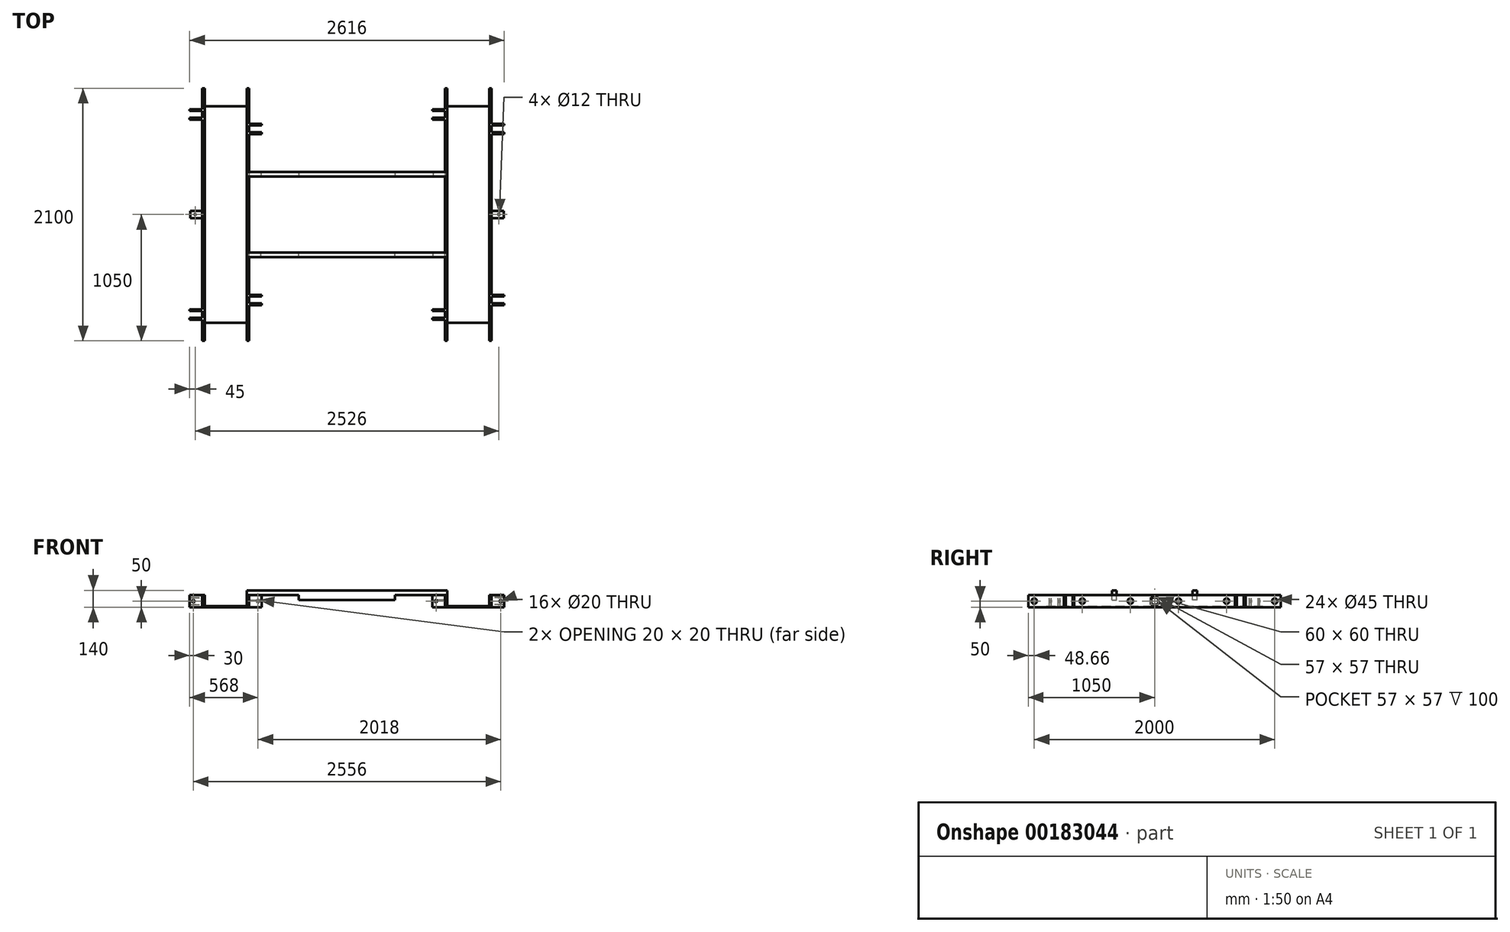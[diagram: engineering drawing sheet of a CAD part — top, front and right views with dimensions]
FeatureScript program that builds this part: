
annotation { "Feature Type Name" : "Feature", "Feature Type Description" : "" }
export const myFeature = defineFeature(function(context is Context, id is Id, definition is map)
    precondition{}
    {
        {
            var Q0;
            Q0=qCreatedBy(makeId("Front.planeOp"),FACE);
            var sketch = newSketch(context, id + "F0", { "sketchPlane" : qUnion([Q0])});
            skLineSegment(sketch, "E0", {"start": v(0, 0) * mm, "end": v(-815, 0) * mm, "construction": true});
            skLineSegment(sketch, "E1", {"start": v(0, 0) * mm, "end": v(815, 0) * mm, "construction": true});
            skLineSegment(sketch, "E2", {"start": v(-834, -90) * mm, "end": v(-1184, -90) * mm});
            skLineSegment(sketch, "E3", {"start": v(-1184, -90) * mm, "end": v(-1184, 0) * mm});
            skLineSegment(sketch, "E4", {"start": v(-1184, 0) * mm, "end": v(-1203, 0) * mm});
            skLineSegment(sketch, "E5", {"start": v(-1203, 0) * mm, "end": v(-1203, -100) * mm});
            skLineSegment(sketch, "E6", {"start": v(-1203, -100) * mm, "end": v(-815, -100) * mm});
            skLineSegment(sketch, "E7", {"start": v(-815, -100) * mm, "end": v(-815, 0) * mm});
            skLineSegment(sketch, "E8", {"start": v(-834, -90) * mm, "end": v(-834, 0) * mm});
            skLineSegment(sketch, "E9", {"start": v(-834, 0) * mm, "end": v(-815, 0) * mm});
            skLineSegment(sketch, "E10.MirrorCS", {"start": v(815, -100) * mm, "end": v(815, 0) * mm});
            skLineSegment(sketch, "E11.MirrorCS", {"start": v(834, -90) * mm, "end": v(834, 0) * mm});
            skLineSegment(sketch, "E12.MirrorCS", {"start": v(1203, -100) * mm, "end": v(815, -100) * mm});
            skLineSegment(sketch, "E13.MirrorCS", {"start": v(834, -90) * mm, "end": v(1184, -90) * mm});
            skLineSegment(sketch, "E14.MirrorCS", {"start": v(1184, -90) * mm, "end": v(1184, 0) * mm});
            skLineSegment(sketch, "E15.MirrorCS", {"start": v(1184, 0) * mm, "end": v(1203, 0) * mm});
            skLineSegment(sketch, "E16.MirrorCS", {"start": v(1203, 0) * mm, "end": v(1203, -100) * mm});
            skLineSegment(sketch, "E17.MirrorCS", {"start": v(834, 0) * mm, "end": v(815, 0) * mm});
            skSolve(sketch);
        }
        {
            var Q0;
            Q0=makeQuery(id+"F0.imprint","IMPRINT",FACE,{"disambiguationData":[TD([[makeQuery(id+"F0.imprint","IMPRINT",EDGE,{"derivedFrom":sQuery(id+"F0.wireOp",EDGE,"E2")}),1.0]])]});
            var Q1;
            Q1=makeQuery(id+"F0.imprint","IMPRINT",FACE,{"disambiguationData":[TD([[makeQuery(id+"F0.imprint","IMPRINT",EDGE,{"derivedFrom":sQuery(id+"F0.wireOp",EDGE,"E10.MirrorCS")}),-1.0]])]});
            extrude(context, id + "F1", {"entities" : qUnion([Q0, Q1]), "endBound" : BoundingType.SYMMETRIC, "depth" : 2100 * mm});
        }
        {
            var Q0;
            Q0=makeQuery(id+"F1.opExtrude","SWEPT_FACE",FACE,{"disambiguationData":[OSD([sQuery(id+"F0.wireOp",EDGE,"E9")])]});
            var sketch = newSketch(context, id + "F2", { "sketchPlane" : qUnion([Q0])});
            skLineSegment(sketch, "E18.bottom", {"start": v(-834, -355) * mm, "end": v(834, -355) * mm});
            skLineSegment(sketch, "E18.top", {"start": v(-834, -315) * mm, "end": v(834, -315) * mm});
            skLineSegment(sketch, "E18.left", {"start": v(834, -315) * mm, "end": v(834, -355) * mm});
            skLineSegment(sketch, "E18.right", {"start": v(-834, -315) * mm, "end": v(-834, -355) * mm});
            skLineSegment(sketch, "E19.bottom", {"start": v(-834, 315) * mm, "end": v(834, 315) * mm});
            skLineSegment(sketch, "E19.top", {"start": v(-834, 355) * mm, "end": v(834, 355) * mm});
            skLineSegment(sketch, "E19.left", {"start": v(-834, 355) * mm, "end": v(-834, 315) * mm});
            skLineSegment(sketch, "E19.right", {"start": v(834, 355) * mm, "end": v(834, 315) * mm});
            skSolve(sketch);
        }
        {
            var Q0;
            {var subQ0=sQuery(id+"F2.wireOp",EDGE,"E18.right");Q0=makeQuery(id+"F2.imprint","IMPRINT",FACE,{"disambiguationData":[TD([[makeQuery(id+"F2.imprint","IMPRINT",EDGE,{"derivedFrom":subQ0}),-1.0]])]});}
            var Q1;
            {var subQ0=sQuery(id+"F2.wireOp",EDGE,"E19.left");Q1=makeQuery(id+"F2.imprint","IMPRINT",FACE,{"disambiguationData":[TD([[makeQuery(id+"F2.imprint","IMPRINT",EDGE,{"derivedFrom":subQ0}),-1.0]])]});}
            var Q2;
            {var subQ0=sQuery(id+"F2.wireOp",EDGE,"E18.left");Q2=makeQuery(id+"F2.imprint","IMPRINT",FACE,{"disambiguationData":[TD([[makeQuery(id+"F2.imprint","IMPRINT",EDGE,{"derivedFrom":subQ0}),-1.0]])]});}
            var Q3;
            {var subQ0=sQuery(id+"F2.wireOp",EDGE,"E19.right");Q3=makeQuery(id+"F2.imprint","IMPRINT",FACE,{"disambiguationData":[TD([[makeQuery(id+"F2.imprint","IMPRINT",EDGE,{"derivedFrom":subQ0}),-1.0]])]});}
            extrude(context, id + "F3", {"entities" : qUnion([Q0, Q1, Q2, Q3]), "operationType" : NewBodyOperationType.ADD, "depth" : 40 * mm});
        }
        {
            var Q0;
            Q0=qCreatedBy(makeId("Top.planeOp"),FACE);
            var sketch = newSketch(context, id + "F4", { "sketchPlane" : qUnion([Q0])});
            skLineSegment(sketch, "E20.bottom", {"start": v(1203, 860) * mm, "end": v(1308, 860) * mm});
            skLineSegment(sketch, "E20.top", {"start": v(1203, 875) * mm, "end": v(1308, 875) * mm});
            skLineSegment(sketch, "E20.left", {"start": v(1203, 860) * mm, "end": v(1203, 875) * mm});
            skLineSegment(sketch, "E20.right", {"start": v(1308, 860) * mm, "end": v(1308, 875) * mm});
            skLineSegment(sketch, "E21.bottom", {"start": v(1203, 803) * mm, "end": v(1308, 803) * mm});
            skLineSegment(sketch, "E21.top", {"start": v(1203, 788) * mm, "end": v(1308, 788) * mm});
            skLineSegment(sketch, "E21.left", {"start": v(1203, 803) * mm, "end": v(1203, 788) * mm});
            skLineSegment(sketch, "E21.right", {"start": v(1308, 803) * mm, "end": v(1308, 788) * mm});
            skLineSegment(sketch, "E22.bottom", {"start": v(815, 755) * mm, "end": v(710, 755) * mm});
            skLineSegment(sketch, "E22.top", {"start": v(815, 740) * mm, "end": v(710, 740) * mm});
            skLineSegment(sketch, "E22.left", {"start": v(815, 755) * mm, "end": v(815, 740) * mm});
            skLineSegment(sketch, "E22.right", {"start": v(710, 755) * mm, "end": v(710, 740) * mm});
            skLineSegment(sketch, "E23.bottom", {"start": v(815, 668) * mm, "end": v(710, 668) * mm});
            skLineSegment(sketch, "E23.top", {"start": v(815, 683) * mm, "end": v(710, 683) * mm});
            skLineSegment(sketch, "E23.left", {"start": v(815, 668) * mm, "end": v(815, 683) * mm});
            skLineSegment(sketch, "E23.right", {"start": v(710, 668) * mm, "end": v(710, 683) * mm});
            skLineSegment(sketch, "E24.MirrorCS", {"start": v(-815, 683) * mm, "end": v(-710, 683) * mm});
            skLineSegment(sketch, "E25.MirrorCS", {"start": v(-815, 668) * mm, "end": v(-710, 668) * mm});
            skLineSegment(sketch, "E26.MirrorCS", {"start": v(-710, 668) * mm, "end": v(-710, 683) * mm});
            skLineSegment(sketch, "E27.MirrorCS", {"start": v(-815, 668) * mm, "end": v(-815, 683) * mm});
            skLineSegment(sketch, "E28.MirrorCS", {"start": v(-815, 755) * mm, "end": v(-815, 740) * mm});
            skLineSegment(sketch, "E29.MirrorCS", {"start": v(-815, 755) * mm, "end": v(-710, 755) * mm});
            skLineSegment(sketch, "E30.MirrorCS", {"start": v(-815, 740) * mm, "end": v(-710, 740) * mm});
            skLineSegment(sketch, "E31.MirrorCS", {"start": v(-710, 755) * mm, "end": v(-710, 740) * mm});
            skLineSegment(sketch, "E32.MirrorCS", {"start": v(-1203, 803) * mm, "end": v(-1203, 788) * mm});
            skLineSegment(sketch, "E33.MirrorCS", {"start": v(-1203, 803) * mm, "end": v(-1308, 803) * mm});
            skLineSegment(sketch, "E34.MirrorCS", {"start": v(-1203, 788) * mm, "end": v(-1308, 788) * mm});
            skLineSegment(sketch, "E35.MirrorCS", {"start": v(-1308, 803) * mm, "end": v(-1308, 788) * mm});
            skLineSegment(sketch, "E36.MirrorCS", {"start": v(-1308, 860) * mm, "end": v(-1308, 875) * mm});
            skLineSegment(sketch, "E37.MirrorCS", {"start": v(-1203, 860) * mm, "end": v(-1308, 860) * mm});
            skLineSegment(sketch, "E38.MirrorCS", {"start": v(-1203, 875) * mm, "end": v(-1308, 875) * mm});
            skLineSegment(sketch, "E39.MirrorCS", {"start": v(-1203, 860) * mm, "end": v(-1203, 875) * mm});
            skLineSegment(sketch, "E40", {"start": v(1009, 1050) * mm, "end": v(1009, 82.46) * mm, "construction": true});
            skLineSegment(sketch, "E41.MirrorCS", {"start": v(815, 860) * mm, "end": v(815, 875) * mm});
            skLineSegment(sketch, "E42.MirrorCS", {"start": v(815, 875) * mm, "end": v(710, 875) * mm});
            skLineSegment(sketch, "E43.MirrorCS", {"start": v(710, 860) * mm, "end": v(710, 875) * mm});
            skLineSegment(sketch, "E44.MirrorCS", {"start": v(815, 860) * mm, "end": v(710, 860) * mm});
            skLineSegment(sketch, "E45.MirrorCS", {"start": v(710, 803) * mm, "end": v(710, 788) * mm});
            skLineSegment(sketch, "E46.MirrorCS", {"start": v(815, 803) * mm, "end": v(710, 803) * mm});
            skLineSegment(sketch, "E47.MirrorCS", {"start": v(815, 788) * mm, "end": v(710, 788) * mm});
            skLineSegment(sketch, "E48.MirrorCS", {"start": v(815, 803) * mm, "end": v(815, 788) * mm});
            skLineSegment(sketch, "E49.MirrorCS", {"start": v(1203, 755) * mm, "end": v(1308, 755) * mm});
            skLineSegment(sketch, "E50.MirrorCS", {"start": v(1203, 740) * mm, "end": v(1308, 740) * mm});
            skLineSegment(sketch, "E51.MirrorCS", {"start": v(1203, 755) * mm, "end": v(1203, 740) * mm});
            skLineSegment(sketch, "E52.MirrorCS", {"start": v(1308, 755) * mm, "end": v(1308, 740) * mm});
            skLineSegment(sketch, "E53.MirrorCS", {"start": v(1308, 668) * mm, "end": v(1308, 683) * mm});
            skLineSegment(sketch, "E54.MirrorCS", {"start": v(1203, 683) * mm, "end": v(1308, 683) * mm});
            skLineSegment(sketch, "E55.MirrorCS", {"start": v(1203, 668) * mm, "end": v(1308, 668) * mm});
            skLineSegment(sketch, "E56.MirrorCS", {"start": v(1203, 668) * mm, "end": v(1203, 683) * mm});
            skLineSegment(sketch, "E57.MirrorCS", {"start": v(-815, 860) * mm, "end": v(-710, 860) * mm});
            skLineSegment(sketch, "E58.MirrorCS", {"start": v(-815, 875) * mm, "end": v(-710, 875) * mm});
            skLineSegment(sketch, "E59.MirrorCS", {"start": v(-815, 860) * mm, "end": v(-815, 875) * mm});
            skLineSegment(sketch, "E60.MirrorCS", {"start": v(-710, 860) * mm, "end": v(-710, 875) * mm});
            skLineSegment(sketch, "E61.MirrorCS", {"start": v(-710, 803) * mm, "end": v(-710, 788) * mm});
            skLineSegment(sketch, "E62.MirrorCS", {"start": v(-815, 803) * mm, "end": v(-710, 803) * mm});
            skLineSegment(sketch, "E63.MirrorCS", {"start": v(-815, 788) * mm, "end": v(-710, 788) * mm});
            skLineSegment(sketch, "E64.MirrorCS", {"start": v(-815, 803) * mm, "end": v(-815, 788) * mm});
            skLineSegment(sketch, "E65.MirrorCS", {"start": v(-1203, 668) * mm, "end": v(-1308, 668) * mm});
            skLineSegment(sketch, "E66.MirrorCS", {"start": v(-1203, 668) * mm, "end": v(-1203, 683) * mm});
            skLineSegment(sketch, "E67.MirrorCS", {"start": v(-1203, 683) * mm, "end": v(-1308, 683) * mm});
            skLineSegment(sketch, "E68.MirrorCS", {"start": v(-1308, 668) * mm, "end": v(-1308, 683) * mm});
            skLineSegment(sketch, "E69.MirrorCS", {"start": v(-1203, 740) * mm, "end": v(-1308, 740) * mm});
            skLineSegment(sketch, "E70.MirrorCS", {"start": v(-1203, 755) * mm, "end": v(-1308, 755) * mm});
            skLineSegment(sketch, "E71.MirrorCS", {"start": v(-1308, 755) * mm, "end": v(-1308, 740) * mm});
            skLineSegment(sketch, "E72.MirrorCS", {"start": v(-1203, 755) * mm, "end": v(-1203, 740) * mm});
            skLineSegment(sketch, "E73.MirrorCS", {"start": v(710, -755) * mm, "end": v(710, -740) * mm});
            skLineSegment(sketch, "E74.MirrorCS", {"start": v(815, -668) * mm, "end": v(815, -683) * mm});
            skLineSegment(sketch, "E75.MirrorCS", {"start": v(710, -803) * mm, "end": v(710, -788) * mm});
            skLineSegment(sketch, "E76.MirrorCS", {"start": v(710, -668) * mm, "end": v(710, -683) * mm});
            skLineSegment(sketch, "E77.MirrorCS", {"start": v(815, -755) * mm, "end": v(815, -740) * mm});
            skLineSegment(sketch, "E78.MirrorCS", {"start": v(815, -860) * mm, "end": v(815, -875) * mm});
            skLineSegment(sketch, "E79.MirrorCS", {"start": v(815, -803) * mm, "end": v(815, -788) * mm});
            skLineSegment(sketch, "E80.MirrorCS", {"start": v(710, -860) * mm, "end": v(710, -875) * mm});
            skLineSegment(sketch, "E81.MirrorCS", {"start": v(815, -668) * mm, "end": v(710, -668) * mm});
            skLineSegment(sketch, "E82.MirrorCS", {"start": v(815, -683) * mm, "end": v(710, -683) * mm});
            skLineSegment(sketch, "E83.MirrorCS", {"start": v(815, -788) * mm, "end": v(710, -788) * mm});
            skLineSegment(sketch, "E84.MirrorCS", {"start": v(815, -740) * mm, "end": v(710, -740) * mm});
            skLineSegment(sketch, "E85.MirrorCS", {"start": v(815, -755) * mm, "end": v(710, -755) * mm});
            skLineSegment(sketch, "E86.MirrorCS", {"start": v(815, -803) * mm, "end": v(710, -803) * mm});
            skLineSegment(sketch, "E87.MirrorCS", {"start": v(815, -860) * mm, "end": v(710, -860) * mm});
            skLineSegment(sketch, "E88.MirrorCS", {"start": v(815, -875) * mm, "end": v(710, -875) * mm});
            skLineSegment(sketch, "E89.MirrorCS", {"start": v(1308, -755) * mm, "end": v(1308, -740) * mm});
            skLineSegment(sketch, "E90.MirrorCS", {"start": v(1308, -803) * mm, "end": v(1308, -788) * mm});
            skLineSegment(sketch, "E91.MirrorCS", {"start": v(1308, -860) * mm, "end": v(1308, -875) * mm});
            skLineSegment(sketch, "E92.MirrorCS", {"start": v(1203, -860) * mm, "end": v(1203, -875) * mm});
            skLineSegment(sketch, "E93.MirrorCS", {"start": v(1203, -755) * mm, "end": v(1203, -740) * mm});
            skLineSegment(sketch, "E94.MirrorCS", {"start": v(1308, -668) * mm, "end": v(1308, -683) * mm});
            skLineSegment(sketch, "E95.MirrorCS", {"start": v(1203, -803) * mm, "end": v(1203, -788) * mm});
            skLineSegment(sketch, "E96.MirrorCS", {"start": v(1203, -668) * mm, "end": v(1203, -683) * mm});
            skLineSegment(sketch, "E97.MirrorCS", {"start": v(1203, -668) * mm, "end": v(1308, -668) * mm});
            skLineSegment(sketch, "E98.MirrorCS", {"start": v(1203, -788) * mm, "end": v(1308, -788) * mm});
            skLineSegment(sketch, "E99.MirrorCS", {"start": v(1203, -803) * mm, "end": v(1308, -803) * mm});
            skLineSegment(sketch, "E100.MirrorCS", {"start": v(1203, -755) * mm, "end": v(1308, -755) * mm});
            skLineSegment(sketch, "E101.MirrorCS", {"start": v(1203, -875) * mm, "end": v(1308, -875) * mm});
            skLineSegment(sketch, "E102.MirrorCS", {"start": v(1203, -860) * mm, "end": v(1308, -860) * mm});
            skLineSegment(sketch, "E103.MirrorCS", {"start": v(1203, -740) * mm, "end": v(1308, -740) * mm});
            skLineSegment(sketch, "E104.MirrorCS", {"start": v(1203, -683) * mm, "end": v(1308, -683) * mm});
            skLineSegment(sketch, "E105.MirrorCS", {"start": v(-1203, -860) * mm, "end": v(-1203, -875) * mm});
            skLineSegment(sketch, "E106.MirrorCS", {"start": v(-1308, -860) * mm, "end": v(-1308, -875) * mm});
            skLineSegment(sketch, "E107.MirrorCS", {"start": v(-1203, -803) * mm, "end": v(-1203, -788) * mm});
            skLineSegment(sketch, "E108.MirrorCS", {"start": v(-1203, -755) * mm, "end": v(-1203, -740) * mm});
            skLineSegment(sketch, "E109.MirrorCS", {"start": v(-1308, -803) * mm, "end": v(-1308, -788) * mm});
            skLineSegment(sketch, "E110.MirrorCS", {"start": v(-1308, -755) * mm, "end": v(-1308, -740) * mm});
            skLineSegment(sketch, "E111.MirrorCS", {"start": v(-1308, -668) * mm, "end": v(-1308, -683) * mm});
            skLineSegment(sketch, "E112.MirrorCS", {"start": v(-1203, -668) * mm, "end": v(-1203, -683) * mm});
            skLineSegment(sketch, "E113.MirrorCS", {"start": v(-1203, -860) * mm, "end": v(-1308, -860) * mm});
            skLineSegment(sketch, "E114.MirrorCS", {"start": v(-1203, -875) * mm, "end": v(-1308, -875) * mm});
            skLineSegment(sketch, "E115.MirrorCS", {"start": v(-1203, -683) * mm, "end": v(-1308, -683) * mm});
            skLineSegment(sketch, "E116.MirrorCS", {"start": v(-1203, -740) * mm, "end": v(-1308, -740) * mm});
            skLineSegment(sketch, "E117.MirrorCS", {"start": v(-1203, -668) * mm, "end": v(-1308, -668) * mm});
            skLineSegment(sketch, "E118.MirrorCS", {"start": v(-1203, -803) * mm, "end": v(-1308, -803) * mm});
            skLineSegment(sketch, "E119.MirrorCS", {"start": v(-1203, -755) * mm, "end": v(-1308, -755) * mm});
            skLineSegment(sketch, "E120.MirrorCS", {"start": v(-1203, -788) * mm, "end": v(-1308, -788) * mm});
            skLineSegment(sketch, "E121.MirrorCS", {"start": v(-815, -803) * mm, "end": v(-815, -788) * mm});
            skLineSegment(sketch, "E122.MirrorCS", {"start": v(-815, -668) * mm, "end": v(-815, -683) * mm});
            skLineSegment(sketch, "E123.MirrorCS", {"start": v(-815, -860) * mm, "end": v(-815, -875) * mm});
            skLineSegment(sketch, "E124.MirrorCS", {"start": v(-710, -755) * mm, "end": v(-710, -740) * mm});
            skLineSegment(sketch, "E125.MirrorCS", {"start": v(-710, -860) * mm, "end": v(-710, -875) * mm});
            skLineSegment(sketch, "E126.MirrorCS", {"start": v(-710, -668) * mm, "end": v(-710, -683) * mm});
            skLineSegment(sketch, "E127.MirrorCS", {"start": v(-815, -755) * mm, "end": v(-815, -740) * mm});
            skLineSegment(sketch, "E128.MirrorCS", {"start": v(-710, -803) * mm, "end": v(-710, -788) * mm});
            skLineSegment(sketch, "E129.MirrorCS", {"start": v(-815, -875) * mm, "end": v(-710, -875) * mm});
            skLineSegment(sketch, "E130.MirrorCS", {"start": v(-815, -740) * mm, "end": v(-710, -740) * mm});
            skLineSegment(sketch, "E131.MirrorCS", {"start": v(-815, -683) * mm, "end": v(-710, -683) * mm});
            skLineSegment(sketch, "E132.MirrorCS", {"start": v(-815, -860) * mm, "end": v(-710, -860) * mm});
            skLineSegment(sketch, "E133.MirrorCS", {"start": v(-815, -755) * mm, "end": v(-710, -755) * mm});
            skLineSegment(sketch, "E134.MirrorCS", {"start": v(-815, -803) * mm, "end": v(-710, -803) * mm});
            skLineSegment(sketch, "E135.MirrorCS", {"start": v(-815, -668) * mm, "end": v(-710, -668) * mm});
            skLineSegment(sketch, "E136.MirrorCS", {"start": v(-815, -788) * mm, "end": v(-710, -788) * mm});
            skLineSegment(sketch, "E137", {"start": v(0, 0) * mm, "end": v(1268.64, 0) * mm, "construction": true});
            skSolve(sketch);
        }
        {
            var Q0;
            Q0=makeQuery(id+"F4.imprint","IMPRINT",FACE,{"disambiguationData":[TD([[makeQuery(id+"F4.imprint","IMPRINT",EDGE,{"derivedFrom":sQuery(id+"F4.wireOp",EDGE,"E37.MirrorCS")}),-1.0]])]});
            var Q1;
            Q1=makeQuery(id+"F4.imprint","IMPRINT",FACE,{"disambiguationData":[TD([[makeQuery(id+"F4.imprint","IMPRINT",EDGE,{"derivedFrom":sQuery(id+"F4.wireOp",EDGE,"E32.MirrorCS")}),-1.0]])]});
            var Q2;
            Q2=makeQuery(id+"F4.imprint","IMPRINT",FACE,{"disambiguationData":[TD([[makeQuery(id+"F4.imprint","IMPRINT",EDGE,{"derivedFrom":sQuery(id+"F4.wireOp",EDGE,"E28.MirrorCS")}),1.0]])]});
            var Q3;
            Q3=makeQuery(id+"F4.imprint","IMPRINT",FACE,{"disambiguationData":[TD([[makeQuery(id+"F4.imprint","IMPRINT",EDGE,{"derivedFrom":sQuery(id+"F4.wireOp",EDGE,"E24.MirrorCS")}),-1.0]])]});
            var Q4;
            Q4=makeQuery(id+"F4.imprint","IMPRINT",FACE,{"disambiguationData":[TD([[makeQuery(id+"F4.imprint","IMPRINT",EDGE,{"derivedFrom":sQuery(id+"F4.wireOp",EDGE,"E41.MirrorCS")}),1.0]])]});
            var Q5;
            Q5=makeQuery(id+"F4.imprint","IMPRINT",FACE,{"disambiguationData":[TD([[makeQuery(id+"F4.imprint","IMPRINT",EDGE,{"derivedFrom":sQuery(id+"F4.wireOp",EDGE,"E45.MirrorCS")}),1.0]])]});
            var Q6;
            Q6=makeQuery(id+"F4.imprint","IMPRINT",FACE,{"disambiguationData":[TD([[makeQuery(id+"F4.imprint","IMPRINT",EDGE,{"derivedFrom":sQuery(id+"F4.wireOp",EDGE,"E49.MirrorCS")}),-1.0]])]});
            var Q7;
            Q7=makeQuery(id+"F4.imprint","IMPRINT",FACE,{"disambiguationData":[TD([[makeQuery(id+"F4.imprint","IMPRINT",EDGE,{"derivedFrom":sQuery(id+"F4.wireOp",EDGE,"E53.MirrorCS")}),1.0]])]});
            var Q8;
            Q8=makeQuery(id+"F4.imprint","IMPRINT",FACE,{"disambiguationData":[TD([[makeQuery(id+"F4.imprint","IMPRINT",EDGE,{"derivedFrom":sQuery(id+"F4.wireOp",EDGE,"E78.MirrorCS")}),-1.0]])]});
            var Q9;
            Q9=makeQuery(id+"F4.imprint","IMPRINT",FACE,{"disambiguationData":[TD([[makeQuery(id+"F4.imprint","IMPRINT",EDGE,{"derivedFrom":sQuery(id+"F4.wireOp",EDGE,"E75.MirrorCS")}),-1.0]])]});
            var Q10;
            Q10=makeQuery(id+"F4.imprint","IMPRINT",FACE,{"disambiguationData":[TD([[makeQuery(id+"F4.imprint","IMPRINT",EDGE,{"derivedFrom":sQuery(id+"F4.wireOp",EDGE,"E94.MirrorCS")}),-1.0]])]});
            var Q11;
            Q11=makeQuery(id+"F4.imprint","IMPRINT",FACE,{"disambiguationData":[TD([[makeQuery(id+"F4.imprint","IMPRINT",EDGE,{"derivedFrom":sQuery(id+"F4.wireOp",EDGE,"E89.MirrorCS")}),1.0]])]});
            var Q12;
            Q12=makeQuery(id+"F4.imprint","IMPRINT",FACE,{"disambiguationData":[TD([[makeQuery(id+"F4.imprint","IMPRINT",EDGE,{"derivedFrom":sQuery(id+"F4.wireOp",EDGE,"E122.MirrorCS")}),1.0]])]});
            var Q13;
            Q13=makeQuery(id+"F4.imprint","IMPRINT",FACE,{"disambiguationData":[TD([[makeQuery(id+"F4.imprint","IMPRINT",EDGE,{"derivedFrom":sQuery(id+"F4.wireOp",EDGE,"E124.MirrorCS")}),1.0]])]});
            var Q14;
            Q14=makeQuery(id+"F4.imprint","IMPRINT",FACE,{"disambiguationData":[TD([[makeQuery(id+"F4.imprint","IMPRINT",EDGE,{"derivedFrom":sQuery(id+"F4.wireOp",EDGE,"E107.MirrorCS")}),1.0]])]});
            var Q15;
            Q15=makeQuery(id+"F4.imprint","IMPRINT",FACE,{"disambiguationData":[TD([[makeQuery(id+"F4.imprint","IMPRINT",EDGE,{"derivedFrom":sQuery(id+"F4.wireOp",EDGE,"E105.MirrorCS")}),-1.0]])]});
            extrude(context, id + "F5", {"entities" : qUnion([Q0, Q1, Q2, Q3, Q4, Q5, Q6, Q7, Q8, Q9, Q10, Q11, Q12, Q13, Q14, Q15]), "operationType" : NewBodyOperationType.ADD, "oppositeDirection" : true, "depth" : 100 * mm});
        }
        {
            var Q0;
            Q0=makeQuery(id+"F5.opExtrude","SWEPT_FACE",FACE,{"disambiguationData":[OSD([sQuery(id+"F4.wireOp",EDGE,"E42.MirrorCS")])]});
            var sketch = newSketch(context, id + "F6", { "sketchPlane" : qUnion([Q0])});
            skCircle(sketch, "E138", {"center": v(-740, -50) * mm, "radius": 10 * mm});
            skPoint(sketch, "E138.centerSnap0", {"position": v(-740, 0) * mm});
            skPoint(sketch, "E138.centerSnap1", {"position": v(-710, -50) * mm});
            skSolve(sketch);
        }
        {
            var Q0;
            Q0=makeQuery(id+"F5.opExtrude","SWEPT_FACE",FACE,{"disambiguationData":[OSD([sQuery(id+"F4.wireOp",EDGE,"E83.MirrorCS")])]});
            var sketch = newSketch(context, id + "F7", { "sketchPlane" : qUnion([Q0])});
            skCircle(sketch, "E139", {"center": v(-740, -50) * mm, "radius": 10 * mm});
            skPoint(sketch, "E139.centerSnap0", {"position": v(-687.5, -50) * mm});
            skPoint(sketch, "E139.centerSnap1", {"position": v(-740, 10) * mm});
            skSolve(sketch);
        }
        {
            var Q0;
            Q0=makeQuery(id+"F5.opExtrude","SWEPT_FACE",FACE,{"disambiguationData":[OSD([sQuery(id+"F4.wireOp",EDGE,"E97.MirrorCS")])]});
            var sketch = newSketch(context, id + "F8", { "sketchPlane" : qUnion([Q0])});
            skCircle(sketch, "E140", {"center": v(-1278, -50) * mm, "radius": 10 * mm});
            skPoint(sketch, "E140.centerSnap0", {"position": v(-1308, -50) * mm});
            skPoint(sketch, "E140.centerSnap1", {"position": v(-1278, 0) * mm});
            skSolve(sketch);
        }
        {
            var Q0;
            Q0=makeQuery(id+"F5.opExtrude","SWEPT_FACE",FACE,{"disambiguationData":[OSD([sQuery(id+"F4.wireOp",EDGE,"E49.MirrorCS")])]});
            var sketch = newSketch(context, id + "F9", { "sketchPlane" : qUnion([Q0])});
            skCircle(sketch, "E141", {"center": v(-1278, -50) * mm, "radius": 10 * mm});
            skPoint(sketch, "E141.centerSnap0", {"position": v(-1308, -50) * mm});
            skPoint(sketch, "E141.centerSnap1", {"position": v(-1278, 0) * mm});
            skSolve(sketch);
        }
        {
            var Q0;
            Q0=makeQuery(id+"F8.imprint","IMPRINT",FACE,{"disambiguationData":[TD([[makeQuery(id+"F8.imprint","IMPRINT",EDGE,{"derivedFrom":sQuery(id+"F8.wireOp",EDGE,"E140")}),1.0]])]});
            var Q1;
            Q1=makeQuery(id+"F7.imprint","IMPRINT",FACE,{"disambiguationData":[TD([[makeQuery(id+"F7.imprint","IMPRINT",EDGE,{"derivedFrom":sQuery(id+"F7.wireOp",EDGE,"E139")}),1.0]])]});
            var Q2;
            Q2=makeQuery(id+"F9.imprint","IMPRINT",FACE,{"disambiguationData":[TD([[makeQuery(id+"F9.imprint","IMPRINT",EDGE,{"derivedFrom":sQuery(id+"F9.wireOp",EDGE,"E141")}),1.0]])]});
            var Q3;
            Q3=makeQuery(id+"F6.imprint","IMPRINT",FACE,{"disambiguationData":[TD([[makeQuery(id+"F6.imprint","IMPRINT",EDGE,{"derivedFrom":sQuery(id+"F6.wireOp",EDGE,"E138")}),1.0]])]});
            extrude(context, id + "F10", {"entities" : qUnion([Q0, Q1, Q2, Q3]), "operationType" : NewBodyOperationType.REMOVE, "oppositeDirection" : true, "depth" : 100 * mm});
        }
        {
            var Q0;
            Q0=makeQuery(id+"F5.opExtrude","SWEPT_FACE",FACE,{"disambiguationData":[OSD([sQuery(id+"F4.wireOp",EDGE,"E120.MirrorCS")])]});
            var sketch = newSketch(context, id + "F11", { "sketchPlane" : qUnion([Q0])});
            skCircle(sketch, "E142", {"center": v(1278, -50) * mm, "radius": 10 * mm});
            skPoint(sketch, "E142.centerSnap0", {"position": v(1308, -50) * mm});
            skPoint(sketch, "E142.centerSnap1", {"position": v(1278, 5) * mm});
            skSolve(sketch);
        }
        {
            var Q0;
            Q0=makeQuery(id+"F5.opExtrude","SWEPT_FACE",FACE,{"disambiguationData":[OSD([sQuery(id+"F4.wireOp",EDGE,"E135.MirrorCS")])]});
            var sketch = newSketch(context, id + "F12", { "sketchPlane" : qUnion([Q0])});
            skCircle(sketch, "E143", {"center": v(740, -50) * mm, "radius": 10 * mm});
            skPoint(sketch, "E143.centerSnap0", {"position": v(710, -50) * mm});
            skPoint(sketch, "E143.centerSnap1", {"position": v(740, 0) * mm});
            skSolve(sketch);
        }
        {
            var Q0;
            Q0=makeQuery(id+"F5.opExtrude","SWEPT_FACE",FACE,{"disambiguationData":[OSD([sQuery(id+"F4.wireOp",EDGE,"E29.MirrorCS")])]});
            var sketch = newSketch(context, id + "F13", { "sketchPlane" : qUnion([Q0])});
            skCircle(sketch, "E144", {"center": v(740, -50) * mm, "radius": 10 * mm});
            skPoint(sketch, "E144.centerSnap0", {"position": v(710, -50) * mm});
            skPoint(sketch, "E144.centerSnap1", {"position": v(740, 0) * mm});
            skSolve(sketch);
        }
        {
            var Q0;
            Q0=makeQuery(id+"F5.opExtrude","SWEPT_FACE",FACE,{"disambiguationData":[OSD([sQuery(id+"F4.wireOp",EDGE,"E38.MirrorCS")])]});
            var sketch = newSketch(context, id + "F14", { "sketchPlane" : qUnion([Q0])});
            skCircle(sketch, "E145", {"center": v(1278, -50) * mm, "radius": 10 * mm});
            skPoint(sketch, "E145.centerSnap0", {"position": v(1308, -50) * mm});
            skPoint(sketch, "E145.centerSnap1", {"position": v(1278, 0) * mm});
            skSolve(sketch);
        }
        {
            var Q0;
            Q0=makeQuery(id+"F13.imprint","IMPRINT",FACE,{"disambiguationData":[TD([[makeQuery(id+"F13.imprint","IMPRINT",EDGE,{"derivedFrom":sQuery(id+"F13.wireOp",EDGE,"E144")}),1.0]])]});
            var Q1;
            Q1=makeQuery(id+"F11.imprint","IMPRINT",FACE,{"disambiguationData":[TD([[makeQuery(id+"F11.imprint","IMPRINT",EDGE,{"derivedFrom":sQuery(id+"F11.wireOp",EDGE,"E142")}),1.0]])]});
            var Q2;
            Q2=makeQuery(id+"F12.imprint","IMPRINT",FACE,{"disambiguationData":[TD([[makeQuery(id+"F12.imprint","IMPRINT",EDGE,{"derivedFrom":sQuery(id+"F12.wireOp",EDGE,"E143")}),1.0]])]});
            var Q3;
            Q3=makeQuery(id+"F14.imprint","IMPRINT",FACE,{"disambiguationData":[TD([[makeQuery(id+"F14.imprint","IMPRINT",EDGE,{"derivedFrom":sQuery(id+"F14.wireOp",EDGE,"E145")}),1.0]])]});
            extrude(context, id + "F15", {"entities" : qUnion([Q0, Q1, Q2, Q3]), "operationType" : NewBodyOperationType.REMOVE, "oppositeDirection" : true, "depth" : 100 * mm});
        }
        {
            var Q0;
            Q0=makeQuery(id+"F3.opExtrude","CAP_FACE",FACE,{"disambiguationData":[OSD([sQuery(id+"F2.wireOp",EDGE,"E19.bottom"),sQuery(id+"F2.wireOp",EDGE,"E19.top"),sQuery(id+"F2.wireOp",EDGE,"E19.left"),sQuery(id+"F2.wireOp",EDGE,"E19.right")])],"isStart":true});
            var sketch = newSketch(context, id + "F16", { "sketchPlane" : qUnion([Q0])});
            skLineSegment(sketch, "E146.bottom", {"start": v(400, -355) * mm, "end": v(-400, -355) * mm});
            skLineSegment(sketch, "E146.top", {"start": v(400, -315) * mm, "end": v(-400, -315) * mm});
            skLineSegment(sketch, "E146.left", {"start": v(400, -355) * mm, "end": v(400, -315) * mm});
            skLineSegment(sketch, "E146.right", {"start": v(-400, -355) * mm, "end": v(-400, -315) * mm});
            skLineSegment(sketch, "E147.MirrorCS", {"start": v(400, 315) * mm, "end": v(-400, 315) * mm});
            skLineSegment(sketch, "E148.MirrorCS", {"start": v(400, 355) * mm, "end": v(-400, 355) * mm});
            skLineSegment(sketch, "E149.MirrorCS", {"start": v(-400, 355) * mm, "end": v(-400, 315) * mm});
            skLineSegment(sketch, "E150.MirrorCS", {"start": v(400, 355) * mm, "end": v(400, 315) * mm});
            skSolve(sketch);
        }
        {
            var Q0;
            Q0=makeQuery(id+"F16.imprint","IMPRINT",FACE,{"disambiguationData":[TD([[makeQuery(id+"F16.imprint","IMPRINT",EDGE,{"derivedFrom":sQuery(id+"F16.wireOp",EDGE,"E146.bottom")}),-1.0]])]});
            var Q1;
            Q1=makeQuery(id+"F16.imprint","IMPRINT",FACE,{"disambiguationData":[TD([[makeQuery(id+"F16.imprint","IMPRINT",EDGE,{"derivedFrom":sQuery(id+"F16.wireOp",EDGE,"E147.MirrorCS")}),-1.0]])]});
            extrude(context, id + "F17", {"entities" : qUnion([Q0, Q1]), "operationType" : NewBodyOperationType.ADD, "depth" : 40 * mm});
        }
        {
            var Q0;
            Q0=makeQuery(id+"F1.opExtrude","SWEPT_FACE",FACE,{"disambiguationData":[OSD([sQuery(id+"F0.wireOp",EDGE,"E2")])]});
            var sketch = newSketch(context, id + "F18", { "sketchPlane" : qUnion([Q0])});
            skLineSegment(sketch, "E151.bottom", {"start": v(-1184, -1050) * mm, "end": v(-834, -1050) * mm});
            skLineSegment(sketch, "E151.top", {"start": v(-1184, -900) * mm, "end": v(-834, -900) * mm});
            skLineSegment(sketch, "E151.left", {"start": v(-1184, -1050) * mm, "end": v(-1184, -900) * mm});
            skLineSegment(sketch, "E151.right", {"start": v(-834, -1050) * mm, "end": v(-834, -900) * mm});
            skLineSegment(sketch, "E152.MirrorCS", {"start": v(-1184, 900) * mm, "end": v(-834, 900) * mm});
            skLineSegment(sketch, "E153.MirrorCS", {"start": v(-834, 1050) * mm, "end": v(-834, 900) * mm});
            skLineSegment(sketch, "E154.MirrorCS", {"start": v(-1184, 1050) * mm, "end": v(-1184, 900) * mm});
            skLineSegment(sketch, "E155.MirrorCS", {"start": v(1184, -900) * mm, "end": v(834, -900) * mm});
            skLineSegment(sketch, "E156.MirrorCS", {"start": v(834, -1050) * mm, "end": v(834, -900) * mm});
            skLineSegment(sketch, "E157.MirrorCS", {"start": v(1184, -1050) * mm, "end": v(834, -1050) * mm});
            skLineSegment(sketch, "E158.MirrorCS", {"start": v(1184, -1050) * mm, "end": v(1184, -900) * mm});
            skLineSegment(sketch, "E159.MirrorCS", {"start": v(1184, 900) * mm, "end": v(834, 900) * mm});
            skLineSegment(sketch, "E160.MirrorCS", {"start": v(834, 1050) * mm, "end": v(834, 900) * mm});
            skLineSegment(sketch, "E161.MirrorCS", {"start": v(1184, 1050) * mm, "end": v(1184, 900) * mm});
            skLineSegment(sketch, "E162.MirrorCS", {"start": v(-1184, 1050) * mm, "end": v(-834, 1050) * mm});
            skLineSegment(sketch, "E163.MirrorCS", {"start": v(1184, 1050) * mm, "end": v(834, 1050) * mm});
            skSolve(sketch);
        }
        {
            var Q0;
            Q0=makeQuery(id+"F18.imprint","IMPRINT",FACE,{"disambiguationData":[TD([[makeQuery(id+"F18.imprint","IMPRINT",EDGE,{"derivedFrom":sQuery(id+"F18.wireOp",EDGE,"E152.MirrorCS")}),1.0]])]});
            var Q1;
            Q1=makeQuery(id+"F18.imprint","IMPRINT",FACE,{"disambiguationData":[TD([[makeQuery(id+"F18.imprint","IMPRINT",EDGE,{"derivedFrom":sQuery(id+"F18.wireOp",EDGE,"E151.bottom")}),-1.0]])]});
            var Q2;
            Q2=makeQuery(id+"F18.imprint","IMPRINT",FACE,{"disambiguationData":[TD([[makeQuery(id+"F18.imprint","IMPRINT",EDGE,{"derivedFrom":sQuery(id+"F18.wireOp",EDGE,"E155.MirrorCS")}),1.0]])]});
            var Q3;
            Q3=makeQuery(id+"F18.imprint","IMPRINT",FACE,{"disambiguationData":[TD([[makeQuery(id+"F18.imprint","IMPRINT",EDGE,{"derivedFrom":sQuery(id+"F18.wireOp",EDGE,"E159.MirrorCS")}),-1.0]])]});
            extrude(context, id + "F19", {"entities" : qUnion([Q0, Q1, Q2, Q3]), "operationType" : NewBodyOperationType.REMOVE, "oppositeDirection" : true, "depth" : 25 * mm});
        }
        {
            var Q0;
            {var subQ8=sQuery(id+"F4.wireOp",EDGE,"E34.MirrorCS");Q0=makeQuery(id+"F5.boolean.opBoolean","SPLIT",FACE,{"disambiguationData":[TD([makeQuery(id+"F5.opExtrude","SWEPT_FACE",FACE,{"disambiguationData":[OSD([subQ8])]})])],"derivedFrom":makeQuery(id+"F1.opExtrude","SWEPT_FACE",FACE,{"disambiguationData":[OSD([sQuery(id+"F0.wireOp",EDGE,"E5")])]})});}
            var sketch = newSketch(context, id + "F20", { "sketchPlane" : qUnion([Q0])});
            skCircle(sketch, "E164", {"center": v(-998.66, -50) * mm, "radius": 22.5 * mm});
            skPoint(sketch, "E164.centerSnap0", {"position": v(-788, -50) * mm});
            skCircle(sketch, "E165.1.0.0", {"center": v(-598.66, -50) * mm, "radius": 22.5 * mm});
            skCircle(sketch, "E165.2.0.0", {"center": v(-198.66, -50) * mm, "radius": 22.5 * mm});
            skLineSegment(sketch, "E165.direction1", {"start": v(-998.66, -50) * mm, "end": v(-598.66, -50) * mm, "construction": true});
            skCircle(sketch, "E166.0.3.0", {"center": v(201.34, -50) * mm, "radius": 22.5 * mm});
            skCircle(sketch, "E166.0.4.0", {"center": v(601.34, -50) * mm, "radius": 22.5 * mm});
            skCircle(sketch, "E166.0.5.0", {"center": v(1001.34, -50) * mm, "radius": 22.5 * mm});
            skSolve(sketch);
        }
        {
            var Q0;
            Q0=makeQuery(id+"F20.imprint","IMPRINT",FACE,{"disambiguationData":[TD([[makeQuery(id+"F20.imprint","IMPRINT",EDGE,{"derivedFrom":sQuery(id+"F20.wireOp",EDGE,"E164")}),1.0]])]});
            var Q1;
            Q1=makeQuery(id+"F20.imprint","IMPRINT",FACE,{"disambiguationData":[TD([[makeQuery(id+"F20.imprint","IMPRINT",EDGE,{"derivedFrom":sQuery(id+"F20.wireOp",EDGE,"E165.1.0.0")}),1.0]])]});
            var Q2;
            Q2=makeQuery(id+"F20.imprint","IMPRINT",FACE,{"disambiguationData":[TD([[makeQuery(id+"F20.imprint","IMPRINT",EDGE,{"derivedFrom":sQuery(id+"F20.wireOp",EDGE,"E165.2.0.0")}),1.0]])]});
            var Q3;
            Q3=makeQuery(id+"F20.imprint","IMPRINT",FACE,{"disambiguationData":[TD([[makeQuery(id+"F20.imprint","IMPRINT",EDGE,{"derivedFrom":sQuery(id+"F20.wireOp",EDGE,"E166.0.3.0")}),1.0]])]});
            var Q4;
            Q4=makeQuery(id+"F20.imprint","IMPRINT",FACE,{"disambiguationData":[TD([[makeQuery(id+"F20.imprint","IMPRINT",EDGE,{"derivedFrom":sQuery(id+"F20.wireOp",EDGE,"E166.0.4.0")}),1.0]])]});
            var Q5;
            Q5=makeQuery(id+"F20.imprint","IMPRINT",FACE,{"disambiguationData":[TD([[makeQuery(id+"F20.imprint","IMPRINT",EDGE,{"derivedFrom":sQuery(id+"F20.wireOp",EDGE,"E166.0.5.0")}),1.0]])]});
            extrude(context, id + "F21", {"entities" : qUnion([Q0, Q1, Q2, Q3, Q4, Q5]), "operationType" : NewBodyOperationType.REMOVE, "endBound" : BoundingType.THROUGH_ALL, "oppositeDirection" : true, "depth" : 25 * mm});
        }
        {
            var Q0;
            {var subQ0=sQuery(id+"F4.wireOp",EDGE,"E55.MirrorCS");Q0=makeQuery(id+"F5.boolean.opBoolean","SPLIT",FACE,{"disambiguationData":[TD([makeQuery(id+"F5.opExtrude","SWEPT_FACE",FACE,{"disambiguationData":[OSD([subQ0])]})])],"derivedFrom":makeQuery(id+"F1.opExtrude","SWEPT_FACE",FACE,{"disambiguationData":[OSD([sQuery(id+"F0.wireOp",EDGE,"E16.MirrorCS")])]})});}
            var sketch = newSketch(context, id + "F22", { "sketchPlane" : qUnion([Q0])});
            skLineSegment(sketch, "E167.bottom", {"start": v(30, -20) * mm, "end": v(-30, -20) * mm});
            skLineSegment(sketch, "E167.top", {"start": v(30, -80) * mm, "end": v(-30, -80) * mm});
            skLineSegment(sketch, "E167.left", {"start": v(30, -20) * mm, "end": v(30, -80) * mm});
            skLineSegment(sketch, "E167.right", {"start": v(-30, -20) * mm, "end": v(-30, -80) * mm});
            skPoint(sketch, "E167.middle", {"position": v(0, -50) * mm});
            skPoint(sketch, "E167.middle.positionSnap0", {"position": v(668, -50) * mm});
            skPoint(sketch, "E167.centerSnap0", {"position": v(668, -50) * mm});
            skLineSegment(sketch, "E168.bottom", {"start": v(28.5, -21.5) * mm, "end": v(-28.5, -21.5) * mm});
            skLineSegment(sketch, "E168.top", {"start": v(28.5, -78.5) * mm, "end": v(-28.5, -78.5) * mm});
            skLineSegment(sketch, "E168.left", {"start": v(28.5, -21.5) * mm, "end": v(28.5, -78.5) * mm});
            skLineSegment(sketch, "E168.right", {"start": v(-28.5, -21.5) * mm, "end": v(-28.5, -78.5) * mm});
            skSolve(sketch);
        }
        {
            var Q0;
            Q0=makeQuery(id+"F22.imprint","IMPRINT",FACE,{"disambiguationData":[TD([[makeQuery(id+"F22.imprint","IMPRINT",EDGE,{"derivedFrom":sQuery(id+"F22.wireOp",EDGE,"E167.bottom")}),1.0]])]});
            extrude(context, id + "F23", {"entities" : qUnion([Q0]), "depth" : 100 * mm});
        }
        {
            var Q0;
            Q0=makeQuery(id+"F23.opExtrude","SWEPT_FACE",FACE,{"disambiguationData":[OSD([sQuery(id+"F22.wireOp",EDGE,"E167.bottom")])]});
            var sketch = newSketch(context, id + "F24", { "sketchPlane" : qUnion([Q0])});
            skCircle(sketch, "E169", {"center": v(1263, 0) * mm, "radius": 6 * mm});
            skPoint(sketch, "E169.centerSnap0", {"position": v(1303, 0) * mm});
            skSolve(sketch);
        }
        {
            var Q0;
            Q0=makeQuery(id+"F24.imprint","IMPRINT",FACE,{"disambiguationData":[TD([[makeQuery(id+"F24.imprint","IMPRINT",EDGE,{"derivedFrom":sQuery(id+"F24.wireOp",EDGE,"E169")}),1.0]])]});
            var Q1;
            Q1=makeQuery(id+"F23.opExtrude","SWEPT_FACE",FACE,{"disambiguationData":[OSD([sQuery(id+"F22.wireOp",EDGE,"E167.top")])]});
            extrude(context, id + "F25", {"entities" : qUnion([Q0]), "operationType" : NewBodyOperationType.REMOVE, "endBound" : BoundingType.UP_TO_SURFACE, "oppositeDirection" : true, "endBoundEntityFace" : qUnion([Q1]), "depth" : 25 * mm});
        }
        {
            var Q0;
            Q0=makeQuery(id+"F23.opExtrude","SWEPT_BODY",BODY,{"disambiguationData":[OSD([sQuery(id+"F22.wireOp",EDGE,"E167.bottom"),sQuery(id+"F22.wireOp",EDGE,"E167.top"),sQuery(id+"F22.wireOp",EDGE,"E167.left"),sQuery(id+"F22.wireOp",EDGE,"E167.right"),sQuery(id+"F22.wireOp",EDGE,"E168.bottom"),sQuery(id+"F22.wireOp",EDGE,"E168.top"),sQuery(id+"F22.wireOp",EDGE,"E168.left"),sQuery(id+"F22.wireOp",EDGE,"E168.right")])]});
            var Q1;
            Q1=qCreatedBy(makeId("Right.planeOp"),FACE);
            mirror(context, id + "F26", {"operationType" : NewBodyOperationType.ADD, "entities" : qUnion([Q0]), "mirrorPlane" : qUnion([Q1])});
        }
        {
            var Q0;
            Q0=makeQuery(id+"F16.imprint","IMPRINT",FACE,{"disambiguationData":[TD([[makeQuery(id+"F16.imprint","IMPRINT",EDGE,{"derivedFrom":sQuery(id+"F16.wireOp",EDGE,"E146.bottom")}),1.0]])]});
            extrude(context, id + "F27", {"entities" : qUnion([Q0]), "operationType" : NewBodyOperationType.ADD, "depth" : 40 * mm});
        }
        {
            var Q0;
            {var subQ0=sQuery(id+"F2.wireOp",EDGE,"E18.top");var subQ1=sQuery(id+"F2.wireOp",EDGE,"E18.bottom");Q0=makeQuery(id+"F17.boolean.opBoolean","SPLIT",FACE,{"disambiguationData":[TD([makeQuery(id+"F1.opExtrude","SWEPT_FACE",FACE,{"disambiguationData":[OSD([sQuery(id+"F0.wireOp",EDGE,"E7")])]})])],"derivedFrom":makeQuery(id+"F3.opExtrude","CAP_FACE",FACE,{"disambiguationData":[OSD([subQ1,subQ0,sQuery(id+"F2.wireOp",EDGE,"E18.left"),sQuery(id+"F2.wireOp",EDGE,"E18.right")])],"isStart":true})});}
            var sketch = newSketch(context, id + "F28", { "sketchPlane" : qUnion([Q0])});
            skLineSegment(sketch, "E170.bottom", {"start": v(-815, 355) * mm, "end": v(-715, 355) * mm});
            skLineSegment(sketch, "E170.top", {"start": v(-815, 315) * mm, "end": v(-715, 315) * mm});
            skLineSegment(sketch, "E170.left", {"start": v(-815, 355) * mm, "end": v(-815, 315) * mm});
            skLineSegment(sketch, "E170.right", {"start": v(-715, 355) * mm, "end": v(-715, 315) * mm});
            skSolve(sketch);
        }
        {
            var Q0;
            Q0=makeQuery(id+"F28.imprint","IMPRINT",FACE,{"disambiguationData":[TD([[makeQuery(id+"F28.imprint","IMPRINT",EDGE,{"derivedFrom":sQuery(id+"F28.wireOp",EDGE,"E170.bottom")}),-1.0]])]});
            extrude(context, id + "F29", {"entities" : qUnion([Q0]), "depth" : 40 * mm});
        }
        {
            var Q0;
            Q0=makeQuery(id+"F29.opExtrude","SWEPT_BODY",BODY,{"disambiguationData":[OSD([sQuery(id+"F28.wireOp",EDGE,"E170.bottom"),sQuery(id+"F28.wireOp",EDGE,"E170.top"),sQuery(id+"F28.wireOp",EDGE,"E170.left"),sQuery(id+"F28.wireOp",EDGE,"E170.right")])]});
            var Q1;
            Q1=qCreatedBy(makeId("Right.planeOp"),FACE);
            mirror(context, id + "F30", {"entities" : qUnion([Q0]), "mirrorPlane" : qUnion([Q1])});
        }
        {
            var Q0;
            Q0=makeQuery(id+"F29.opExtrude","SWEPT_BODY",BODY,{"disambiguationData":[OSD([sQuery(id+"F28.wireOp",EDGE,"E170.bottom"),sQuery(id+"F28.wireOp",EDGE,"E170.top"),sQuery(id+"F28.wireOp",EDGE,"E170.left"),sQuery(id+"F28.wireOp",EDGE,"E170.right")])]});
            var Q1;
            Q1=makeQuery(id+"F30.opPattern","COPY",BODY,{"derivedFrom":makeQuery(id+"F29.opExtrude","SWEPT_BODY",BODY,{"disambiguationData":[OSD([sQuery(id+"F28.wireOp",EDGE,"E170.bottom"),sQuery(id+"F28.wireOp",EDGE,"E170.top"),sQuery(id+"F28.wireOp",EDGE,"E170.left"),sQuery(id+"F28.wireOp",EDGE,"E170.right")])]}),"instanceName":"1"});
            var Q2;
            Q2=qCreatedBy(makeId("Front.planeOp"),FACE);
            mirror(context, id + "F31", {"operationType" : NewBodyOperationType.ADD, "entities" : qUnion([Q0, Q1]), "mirrorPlane" : qUnion([Q2])});
        }
    });
